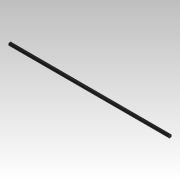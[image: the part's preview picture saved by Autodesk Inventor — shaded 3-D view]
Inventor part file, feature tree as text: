
AUTODESK INVENTOR PART (.ipt)
format: ipt  version: 2020 (Build 240168000, 168)  size: 86,016 bytes
history: native  units: mm
features: revolve x1, chamfer x1, sketch x1
ambient origin geometry x8: Origin, YZ Plane, XZ Plane, XY Plane, X Axis, Y Axis, Z Axis, Center Point
bodies: Solid1 (feature_tree)
feature tree (3):
  revolve  "Revolution1"  [1 undecoded]
  chamfer  "Chamfer1"  Distance=100.0mm
  sketch  "Sketch1"  dims[d0=0.5mm d1=1.0mm d2=100.0mm d3=90.0deg d4=0.25mm d5=2.0mm d6=45.0deg]
note: 1 required parameter value undecoded (feature->parameter linkage not recoverable at this tier; creation-order binding heuristic only, values carry confidence <= 0.55)
